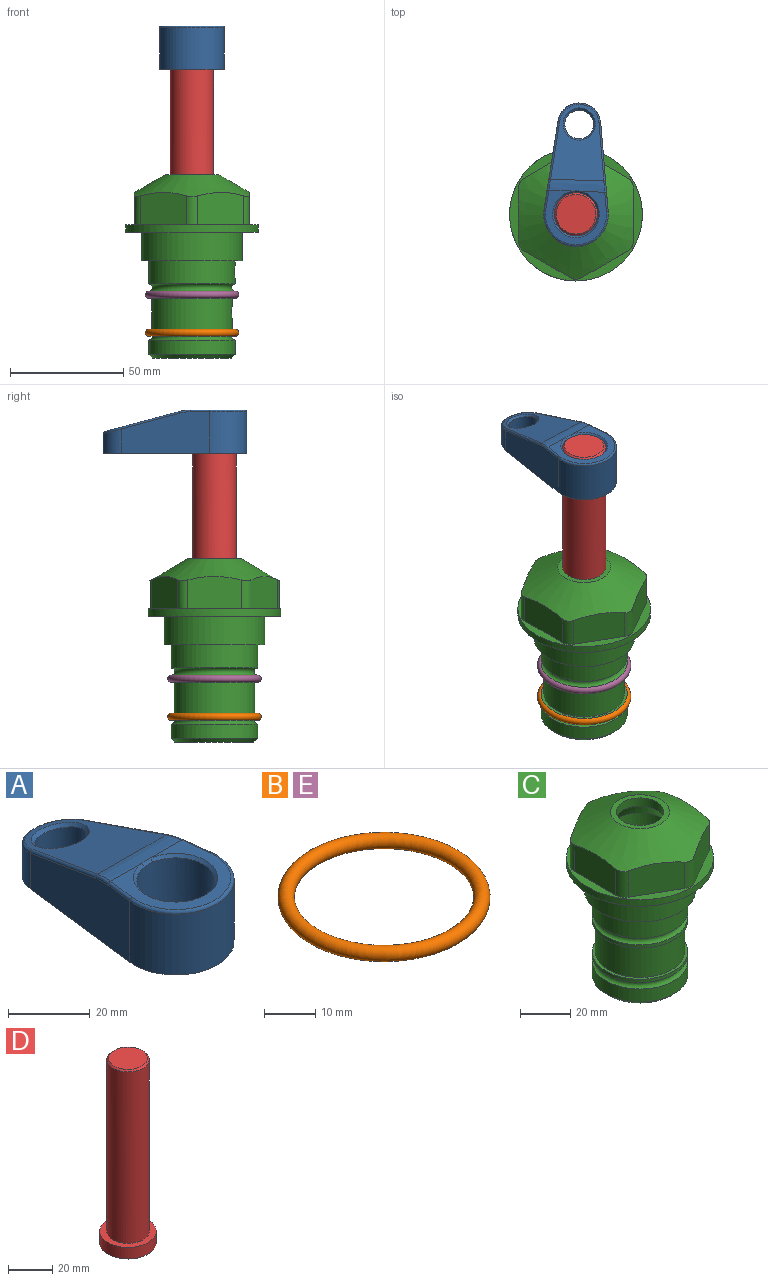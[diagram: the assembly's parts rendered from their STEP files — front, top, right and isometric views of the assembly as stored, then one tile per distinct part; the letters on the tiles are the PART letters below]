
ASSEMBLY  parts=5 mates=4
PART A: 31 faces, bbox 31.7x65.5x19.8 mm
  f0: plane 39.12x18.26mm, normal (0.99,0.12,0), area 612.2mm2, adj f1,f4,f7,f11,f13,f15
  f1: cylinder r=9.53mm len=18.91mm, axis (0,0,-1), area 296.1mm2, adj f0,f2,f7,f17
  f2: plane 39.12x18.26mm, normal (-0.99,0.12,0), area 612.2mm2, adj f1,f4,f7,f12,f14,f16
  f3: cylinder r=6.35mm len=12.7mm, axis (0,0,-1), area 362.4mm2, adj f7,f18
  f4: cylinder r=14.29mm len=28.58mm, axis (0,0,-1), area 882.2mm2, adj f0,f2,f7,f10
  f5: cylinder r=9.53mm len=19.05mm, axis (0,0,-1), area 1092.6mm2, adj f7,f19,f20
  f6: plane 26.99x23.69mm, normal (0,0,1), area 216.2mm2, adj f9,f10,f11,f12,f19
  f7: plane 63.5x28.58mm, normal (0,0,-1), area 661.8mm2, adj f0,f1,f2,f3,f4,f5,f22,f23
  f8: plane 33.52x23.6mm, normal (0,0.26,0.97), area 486mm2, adj f9,f15,f16,f17,f18
  f9: cylinder r=19.05mm len=24.72mm, axis (1,0,0), area 120.4mm2, adj f6,f8,f13,f14,f20
  f10: torus R=13.49mm, axis (0,0,1), area 59mm2, adj f4,f6,f11,f12
  f11: cylinder r=0.79mm len=8.67mm, axis (0.12,-0.99,0), area 10.8mm2, adj f0,f6,f10,f13
  f12: cylinder r=0.79mm len=8.67mm, axis (0.12,0.99,0), area 10.8mm2, adj f2,f6,f10,f14
  f13: bspline ~4.95x1.42mm, area 6.1mm2, adj f0,f9,f11,f15
  f14: bspline ~4.95x1.42mm, area 6.1mm2, adj f2,f9,f12,f16
  f15: cylinder r=0.79mm len=25.95mm, axis (0.12,-0.96,0.26), area 32.9mm2, adj f0,f8,f13,f17
  f16: cylinder r=0.79mm len=25.95mm, axis (0.12,0.96,-0.26), area 32.9mm2, adj f2,f8,f14,f17
  f17: bspline ~18.91x8.38mm, area 30mm2, adj f1,f8,f15,f16
  f18: bspline ~14.29x14.29mm, area 48.3mm2, adj f3,f8
  f19: cone r=9.53mm half-angle=45deg, axis (0,0,1), area 66.5mm2, adj f5,f6,f20
  f20: bspline ~3.22x0.96mm, area 3.5mm2, adj f5,f9,f19
  f21: plane 2.75x2.72mm, normal (0,0,-1), area 2.9mm2, adj f23,f25,f28
  f22: plane 23.05x15.88mm, normal (-0.99,-0.12,0), area 323.6mm2, adj f7,f25,f26,f27,f28,f29
  f23: plane 23.05x15.88mm, normal (0.99,-0.12,0), area 323.6mm2, adj f7,f21,f25,f27,f28,f30
  f24: cylinder r=9.53mm len=10.69mm, axis (0,0,-1), area 114.7mm2, adj f7,f27,f29,f30
  f25: cylinder r=12.7mm len=20.59mm, axis (0,0,-1), area 381.1mm2, adj f7,f21,f22,f23,f26,f28
  f26: plane 2.75x2.72mm, normal (0,0,-1), area 2.9mm2, adj f22,f25,f28
  f27: plane 19.72x18.37mm, normal (0,-0.26,-0.97), area 291.8mm2, adj f22,f23,f24,f28,f29,f30
  f28: cylinder r=15.88mm len=19.92mm, axis (1,0,0), area 54.8mm2, adj f21,f22,f23,f25,f26,f27
  f29: cylinder r=1.59mm len=11mm, axis (0,0,-1), area 34.7mm2, adj f7,f22,f24,f27
  f30: cylinder r=1.59mm len=11mm, axis (0,0,-1), area 34.7mm2, adj f7,f23,f24,f27
PART B: 1 faces, bbox 44.7x44.7x3.2 mm
  f0: torus R=19.05mm, axis (0,0,1), area 1193.9mm2
PART C: 36 faces, bbox 58.7x58.7x81 mm
  f0: cylinder r=17.78mm len=35.56mm, axis (0,0,1), area 1670.8mm2, adj f23,f24,f31
  f1: cylinder r=19.05mm len=38.1mm, axis (0,0,1), area 1191.9mm2, adj f26,f27,f30
  f2: plane 58.66x58.66mm, normal (0,0,-1), area 1150.6mm2, adj f3,f28
  f3: cylinder r=29.33mm len=58.66mm, axis (0,0,-1), area 585.1mm2, adj f2,f4
  f4: plane 58.66x58.66mm, normal (0,0,1), area 475.9mm2, adj f3,f5,f6,f7,f8,f9,f10,f11
  f5: plane 20.32x14.34mm, normal (-0.5,0.87,0), area 324.4mm2, adj f4,f15,f16,f17
  f6: plane 20.32x14.34mm, normal (0.5,0.87,0), area 324.4mm2, adj f4,f14,f15,f17
  f7: plane 23.48x14.34mm, normal (1,0,0), area 324.4mm2, adj f4,f13,f14,f17
  f8: plane 20.32x14.34mm, normal (0.5,-0.87,0), area 324.4mm2, adj f4,f12,f13,f17
  f9: plane 20.32x14.34mm, normal (-0.5,-0.87,0), area 324.4mm2, adj f4,f11,f12,f17
  f10: plane 23.48x14.34mm, normal (-1,0,0), area 324.4mm2, adj f4,f11,f16,f17
  f11: cylinder r=5.08mm len=12.85mm, axis (0,0,-1), area 67.2mm2, adj f4,f9,f10,f17
  f12: cylinder r=5.08mm len=12.85mm, axis (0,0,-1), area 67.2mm2, adj f4,f8,f9,f17
  f13: cylinder r=5.08mm len=12.85mm, axis (0,0,-1), area 67.2mm2, adj f4,f7,f8,f17
  f14: cylinder r=5.08mm len=12.85mm, axis (0,0,-1), area 67.2mm2, adj f4,f6,f7,f17
  f15: cylinder r=5.08mm len=12.85mm, axis (0,0,-1), area 67.2mm2, adj f4,f5,f6,f17
  f16: cylinder r=5.08mm len=12.85mm, axis (0,0,-1), area 67.2mm2, adj f4,f5,f10,f17
  f17: cone r=11.73mm half-angle=60deg, axis (0,0,-1), area 2071.8mm2, adj f5,f6,f7,f8,f9,f10,f11,f12
  f18: plane 23.46x23.46mm, normal (0,0,1), area 147.4mm2, adj f17,f35
  f19: plane 34.93x34.93mm, normal (0,0,-1), area 958mm2, adj f29
  f20: cylinder r=19.05mm len=38.1mm, axis (0,0,1), area 760.1mm2, adj f21,f29
  f21: torus R=19.05mm, axis (0,0,1), area 565.3mm2, adj f20,f22
  f22: cylinder r=19.05mm len=38.1mm, axis (0,0,1), area 190mm2, adj f21,f23
  f23: plane 38.1x38.1mm, normal (0,0,1), area 146.9mm2, adj f0,f22
  f24: plane 38.1x38.1mm, normal (0,0,-1), area 146.9mm2, adj f0,f25
  f25: cylinder r=19.05mm len=38.1mm, axis (0,0,1), area 190mm2, adj f24,f26
  f26: torus R=19.05mm, axis (0,0,1), area 565.3mm2, adj f1,f25
  f27: plane 44.45x44.45mm, normal (0,0,-1), area 411.7mm2, adj f1,f28
  f28: cylinder r=22.23mm len=44.45mm, axis (0,0,1), area 1773.5mm2, adj f2,f27
  f29: cone r=19.05mm half-angle=45deg, axis (0,0,1), area 257.5mm2, adj f19,f20
  f30: cylinder r=3.17mm len=6.75mm, axis (-1,0,0), area 128mm2, adj f1,f33
  f31: cylinder r=3.17mm len=6.35mm, axis (-1,0,0), area 102.5mm2, adj f0,f33
  f32: plane 25.4x25.4mm, normal (0,0,1), area 506.7mm2, adj f33
  f33: cylinder r=12.7mm len=66.42mm, axis (0,0,-1), area 5236.2mm2, adj f30,f31,f32,f34
  f34: cone r=9.53mm half-angle=30deg, axis (0,0,-1), area 443.4mm2, adj f33,f35
  f35: cylinder r=9.53mm len=19.05mm, axis (0,0,-1), area 240.9mm2, adj f18,f34
PART D: 6 faces, bbox 25.4x25.4x101.6 mm
  f0: plane 17.46x17.46mm, normal (0,0,1), area 239.5mm2, adj f5
  f1: plane 25.4x25.4mm, normal (0,0,-1), area 506.7mm2, adj f2
  f2: cylinder r=12.7mm len=25.4mm, axis (0,0,1), area 506.7mm2, adj f1,f3
  f3: plane 25.4x25.4mm, normal (0,0,1), area 221.7mm2, adj f2,f4
  f4: cylinder r=9.53mm len=94.46mm, axis (0,0,1), area 5653mm2, adj f3,f5
  f5: cone r=8.73mm half-angle=45deg, axis (0,0,-1), area 64.4mm2, adj f0,f4
PART E: same geometry as B
PLACE A rot(axis=(0,0,-1),2.1deg) t=(0,0,27.55)mm
PLACE B t=(0,0,-20)mm
PLACE C at identity fixed
PLACE D rot(axis=(0,0,-1),2.1deg) t=(0,0,27.55)mm
PLACE E t=(0,0,-3.18)mm
MATE fastened E.f0 <-> C.f0  axis (0,0,1) through (0,0,-27.69)mm
MATE cylindrical D.f2 <-> C.f0  axis (0,0,-1) through (0,0,-10.55)mm
MATE fastened B.f0 <-> C.f0  axis (0,0,1) through (0,0,-44.51)mm
MATE fastened D.f2 <-> A.f4  axis (0,0,1) through (0,0,91.05)mm
